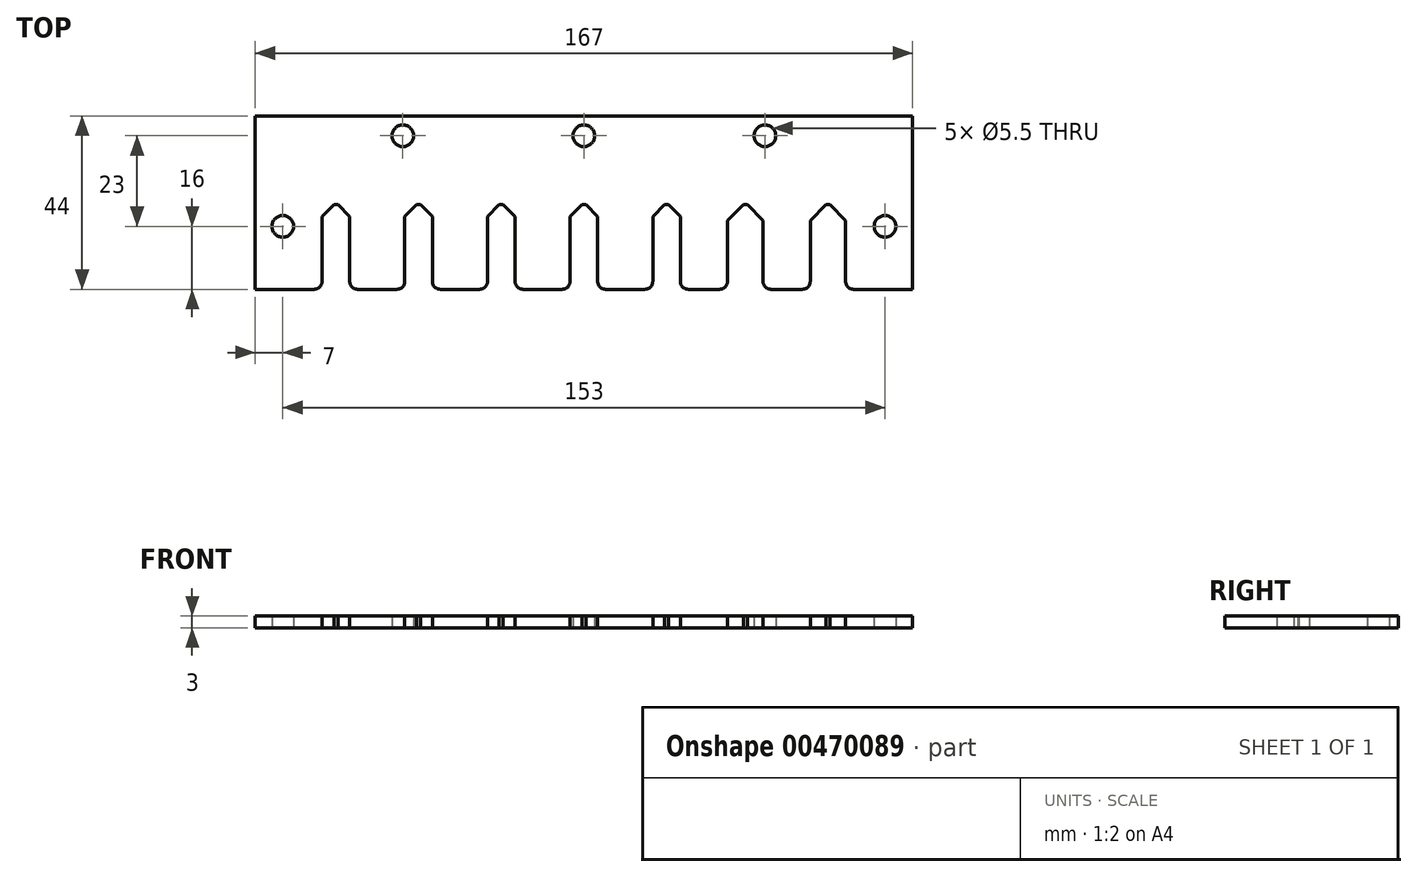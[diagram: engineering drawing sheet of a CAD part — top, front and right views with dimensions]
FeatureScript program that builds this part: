
annotation { "Feature Type Name" : "Feature", "Feature Type Description" : "" }
export const myFeature = defineFeature(function(context is Context, id is Id, definition is map)
    precondition{}
    {
        {
            var Q0;
            Q0=qCreatedBy(makeId("Top.planeOp"),FACE);
            var sketch = newSketch(context, id + "F0", { "sketchPlane" : qUnion([Q0])});
            skLineSegment(sketch, "E0", {"start": v(0, 0) * mm, "end": v(0, 44) * mm});
            skLineSegment(sketch, "E1", {"start": v(0, 44) * mm, "end": v(167, 44) * mm});
            skLineSegment(sketch, "E2", {"start": v(167, 44) * mm, "end": v(167, 0) * mm});
            skLineSegment(sketch, "E3", {"start": v(167, 0) * mm, "end": v(152, 0) * mm});
            skLineSegment(sketch, "E4", {"start": v(150, 2) * mm, "end": v(150, 18) * mm});
            skLineSegment(sketch, "E5", {"start": v(146, 22) * mm, "end": v(145, 22) * mm});
            skLineSegment(sketch, "E6", {"start": v(141, 18) * mm, "end": v(141, 2) * mm});
            skLineSegment(sketch, "E7", {"start": v(139, 0) * mm, "end": v(131, 0) * mm});
            skLineSegment(sketch, "E8", {"start": v(129, 2) * mm, "end": v(129, 18) * mm});
            skLineSegment(sketch, "E9", {"start": v(125, 22) * mm, "end": v(124, 22) * mm});
            skLineSegment(sketch, "E10", {"start": v(120, 18) * mm, "end": v(120, 2) * mm});
            skLineSegment(sketch, "E11", {"start": v(118, 0) * mm, "end": v(110, 0) * mm});
            skLineSegment(sketch, "E12", {"start": v(108, 2) * mm, "end": v(108, 19) * mm});
            skLineSegment(sketch, "E13", {"start": v(105, 22) * mm, "end": v(104, 22) * mm});
            skLineSegment(sketch, "E14", {"start": v(101, 19) * mm, "end": v(101, 2) * mm});
            skLineSegment(sketch, "E15", {"start": v(99, 0) * mm, "end": v(89, 0) * mm});
            skLineSegment(sketch, "E16", {"start": v(87, 2) * mm, "end": v(87, 19) * mm});
            skLineSegment(sketch, "E17", {"start": v(84, 22) * mm, "end": v(83, 22) * mm});
            skLineSegment(sketch, "E18", {"start": v(80, 19) * mm, "end": v(80, 2) * mm});
            skLineSegment(sketch, "E19", {"start": v(78, 0) * mm, "end": v(68, 0) * mm});
            skLineSegment(sketch, "E20", {"start": v(66, 2) * mm, "end": v(66, 19) * mm});
            skLineSegment(sketch, "E21", {"start": v(63, 22) * mm, "end": v(62, 22) * mm});
            skLineSegment(sketch, "E22", {"start": v(59, 19) * mm, "end": v(59, 2) * mm});
            skLineSegment(sketch, "E23", {"start": v(57, 0) * mm, "end": v(47, 0) * mm});
            skLineSegment(sketch, "E24", {"start": v(45, 2) * mm, "end": v(45, 19) * mm});
            skLineSegment(sketch, "E25", {"start": v(42, 22) * mm, "end": v(41, 22) * mm});
            skLineSegment(sketch, "E26", {"start": v(38, 19) * mm, "end": v(38, 2) * mm});
            skLineSegment(sketch, "E27", {"start": v(36, 0) * mm, "end": v(26, 0) * mm});
            skLineSegment(sketch, "E28", {"start": v(24, 2) * mm, "end": v(24, 19) * mm});
            skLineSegment(sketch, "E29", {"start": v(21, 22) * mm, "end": v(20, 22) * mm});
            skLineSegment(sketch, "E30", {"start": v(17, 19) * mm, "end": v(17, 2) * mm});
            skLineSegment(sketch, "E31", {"start": v(15, 0) * mm, "end": v(0, 0) * mm});
            skCircle(sketch, "E32", {"center": v(160, 16) * mm, "radius": 2.75 * mm});
            skCircle(sketch, "E33", {"center": v(129.5, 39) * mm, "radius": 2.75 * mm});
            skCircle(sketch, "E34", {"center": v(37.5, 39) * mm, "radius": 2.75 * mm});
            skPoint(sketch, "E35.centerSnap0", {"position": v(20.5, 22) * mm});
            skCircle(sketch, "E36", {"center": v(20.5, 19) * mm, "radius": 3 * mm, "construction": true});
            skLineSegment(sketch, "E37", {"start": v(20.5, 22) * mm, "end": v(20.5, 0) * mm, "construction": true});
            skCircle(sketch, "E38", {"center": v(20.5, 19) * mm, "radius": 5 * mm, "construction": true});
            skCircle(sketch, "E39", {"center": v(41.5, 19) * mm, "radius": 3 * mm, "construction": true});
            skPoint(sketch, "E39.centerSnap0", {"position": v(41.5, 22) * mm});
            skCircle(sketch, "E40", {"center": v(41.5, 19) * mm, "radius": 5 * mm, "construction": true});
            skPoint(sketch, "E41.visualSharp", {"position": v(17, 0) * mm});
            skArc(sketch, "E41.filletArc", {"start": v(15, 0) * mm, "mid": v(16.41, 0.59) * mm, "end": v(17, 2) * mm});
            skPoint(sketch, "E42.visualSharp", {"position": v(24, 0) * mm});
            skArc(sketch, "E42.filletArc", {"start": v(24, 2) * mm, "mid": v(24.59, 0.59) * mm, "end": v(26, 0) * mm});
            skPoint(sketch, "E43.visualSharp", {"position": v(38, 0) * mm});
            skArc(sketch, "E43.filletArc", {"start": v(36, 0) * mm, "mid": v(37.41, 0.59) * mm, "end": v(38, 2) * mm});
            skPoint(sketch, "E44.visualSharp", {"position": v(45, 0) * mm});
            skArc(sketch, "E44.filletArc", {"start": v(45, 2) * mm, "mid": v(45.59, 0.59) * mm, "end": v(47, 0) * mm});
            skPoint(sketch, "E45.visualSharp", {"position": v(59, 0) * mm});
            skArc(sketch, "E45.filletArc", {"start": v(57, 0) * mm, "mid": v(58.41, 0.59) * mm, "end": v(59, 2) * mm});
            skPoint(sketch, "E46.visualSharp", {"position": v(66, 0) * mm});
            skArc(sketch, "E46.filletArc", {"start": v(66, 2) * mm, "mid": v(66.59, 0.59) * mm, "end": v(68, 0) * mm});
            skPoint(sketch, "E47.visualSharp", {"position": v(80, 0) * mm});
            skArc(sketch, "E47.filletArc", {"start": v(78, 0) * mm, "mid": v(79.41, 0.59) * mm, "end": v(80, 2) * mm});
            skPoint(sketch, "E48.visualSharp", {"position": v(87, 0) * mm});
            skArc(sketch, "E48.filletArc", {"start": v(87, 2) * mm, "mid": v(87.59, 0.59) * mm, "end": v(89, 0) * mm});
            skPoint(sketch, "E49.visualSharp", {"position": v(101, 0) * mm});
            skArc(sketch, "E49.filletArc", {"start": v(99, 0) * mm, "mid": v(100.41, 0.59) * mm, "end": v(101, 2) * mm});
            skPoint(sketch, "E50.visualSharp", {"position": v(108, 0) * mm});
            skArc(sketch, "E50.filletArc", {"start": v(108, 2) * mm, "mid": v(108.59, 0.59) * mm, "end": v(110, 0) * mm});
            skPoint(sketch, "E51.visualSharp", {"position": v(120, 0) * mm});
            skArc(sketch, "E51.filletArc", {"start": v(118, 0) * mm, "mid": v(119.41, 0.59) * mm, "end": v(120, 2) * mm});
            skPoint(sketch, "E52.visualSharp", {"position": v(129, 0) * mm});
            skArc(sketch, "E52.filletArc", {"start": v(129, 2) * mm, "mid": v(129.59, 0.59) * mm, "end": v(131, 0) * mm});
            skPoint(sketch, "E53.visualSharp", {"position": v(141, 0) * mm});
            skArc(sketch, "E53.filletArc", {"start": v(139, 0) * mm, "mid": v(140.41, 0.59) * mm, "end": v(141, 2) * mm});
            skPoint(sketch, "E54.visualSharp", {"position": v(150, 0) * mm});
            skArc(sketch, "E54.filletArc", {"start": v(150, 2) * mm, "mid": v(150.59, 0.59) * mm, "end": v(152, 0) * mm});
            skCircle(sketch, "E55", {"center": v(7, 16) * mm, "radius": 2.75 * mm});
            skPoint(sketch, "E56.visualSharp", {"position": v(45, 22) * mm});
            skArc(sketch, "E56.filletArc", {"start": v(45, 19) * mm, "mid": v(44.12, 21.12) * mm, "end": v(42, 22) * mm});
            skPoint(sketch, "E57.visualSharp", {"position": v(38, 22) * mm});
            skArc(sketch, "E57.filletArc", {"start": v(41, 22) * mm, "mid": v(38.88, 21.12) * mm, "end": v(38, 19) * mm});
            skPoint(sketch, "E58.visualSharp", {"position": v(24, 22) * mm});
            skArc(sketch, "E58.filletArc", {"start": v(24, 19) * mm, "mid": v(23.12, 21.12) * mm, "end": v(21, 22) * mm});
            skPoint(sketch, "E59.visualSharp", {"position": v(17, 22) * mm});
            skArc(sketch, "E59.filletArc", {"start": v(20, 22) * mm, "mid": v(17.88, 21.12) * mm, "end": v(17, 19) * mm});
            skPoint(sketch, "E60.visualSharp", {"position": v(59, 22) * mm});
            skArc(sketch, "E60.filletArc", {"start": v(62, 22) * mm, "mid": v(59.88, 21.12) * mm, "end": v(59, 19) * mm});
            skPoint(sketch, "E61.visualSharp", {"position": v(66, 22) * mm});
            skArc(sketch, "E61.filletArc", {"start": v(66, 19) * mm, "mid": v(65.12, 21.12) * mm, "end": v(63, 22) * mm});
            skPoint(sketch, "E62.visualSharp", {"position": v(80, 22) * mm});
            skArc(sketch, "E62.filletArc", {"start": v(83, 22) * mm, "mid": v(80.88, 21.12) * mm, "end": v(80, 19) * mm});
            skPoint(sketch, "E63.visualSharp", {"position": v(87, 22) * mm});
            skArc(sketch, "E63.filletArc", {"start": v(87, 19) * mm, "mid": v(86.12, 21.12) * mm, "end": v(84, 22) * mm});
            skPoint(sketch, "E64.visualSharp", {"position": v(101, 22) * mm});
            skArc(sketch, "E64.filletArc", {"start": v(104, 22) * mm, "mid": v(101.88, 21.12) * mm, "end": v(101, 19) * mm});
            skPoint(sketch, "E65.visualSharp", {"position": v(108, 22) * mm});
            skArc(sketch, "E65.filletArc", {"start": v(108, 19) * mm, "mid": v(107.12, 21.12) * mm, "end": v(105, 22) * mm});
            skPoint(sketch, "E66", {"position": v(62.5, 22) * mm});
            skPoint(sketch, "E67", {"position": v(83.5, 22) * mm});
            skCircle(sketch, "E68", {"center": v(83.5, 19) * mm, "radius": 3 * mm, "construction": true});
            skCircle(sketch, "E69", {"center": v(83.5, 19) * mm, "radius": 5 * mm, "construction": true});
            skCircle(sketch, "E70", {"center": v(62.5, 19) * mm, "radius": 3 * mm, "construction": true});
            skCircle(sketch, "E71", {"center": v(62.5, 19) * mm, "radius": 5 * mm, "construction": true});
            skPoint(sketch, "E72", {"position": v(104.5, 22) * mm});
            skCircle(sketch, "E73", {"center": v(104.5, 19) * mm, "radius": 3 * mm, "construction": true});
            skCircle(sketch, "E74", {"center": v(104.5, 19) * mm, "radius": 5 * mm, "construction": true});
            skCircle(sketch, "E75", {"center": v(145.5, 19) * mm, "radius": 3 * mm, "construction": true});
            skCircle(sketch, "E76", {"center": v(145.5, 19) * mm, "radius": 7 * mm, "construction": true});
            skPoint(sketch, "E77.visualSharp", {"position": v(141, 22) * mm});
            skArc(sketch, "E77.filletArc", {"start": v(145, 22) * mm, "mid": v(142.17, 20.83) * mm, "end": v(141, 18) * mm});
            skArc(sketch, "E78.filletArc", {"start": v(150, 18) * mm, "mid": v(148.83, 20.83) * mm, "end": v(146, 22) * mm});
            skPoint(sketch, "E79.visualSharp", {"position": v(129, 22) * mm});
            skArc(sketch, "E79.filletArc", {"start": v(129, 18) * mm, "mid": v(127.83, 20.83) * mm, "end": v(125, 22) * mm});
            skPoint(sketch, "E80.visualSharp", {"position": v(120, 22) * mm});
            skArc(sketch, "E80.filletArc", {"start": v(124, 22) * mm, "mid": v(121.17, 20.83) * mm, "end": v(120, 18) * mm});
            skPoint(sketch, "E81", {"position": v(145.5, 22) * mm});
            skCircle(sketch, "E82", {"center": v(124.5, 19) * mm, "radius": 3 * mm, "construction": true});
            skPoint(sketch, "E82.centerSnap0", {"position": v(124.5, 22) * mm});
            skCircle(sketch, "E83", {"center": v(124.5, 19) * mm, "radius": 7 * mm, "construction": true});
            skLineSegment(sketch, "E84", {"start": v(83.5, 44) * mm, "end": v(83.5, 31) * mm, "construction": true});
            skCircle(sketch, "E85", {"center": v(83.5, 39) * mm, "radius": 2.75 * mm});
            skLineSegment(sketch, "E86", {"start": v(20.5, 22) * mm, "end": v(17, 18.5) * mm});
            skLineSegment(sketch, "E87", {"start": v(20.5, 22) * mm, "end": v(24, 18.5) * mm});
            skCircle(sketch, "E88", {"center": v(20.5, 17.76) * mm, "radius": 3 * mm, "construction": true});
            skLineSegment(sketch, "E89", {"start": v(20, 21.5) * mm, "end": v(21, 21.5) * mm});
            skLineSegment(sketch, "E90.1.0.0", {"start": v(41.5, 22) * mm, "end": v(38, 18.5) * mm});
            skLineSegment(sketch, "E90.1.0.1", {"start": v(41.5, 22) * mm, "end": v(45, 18.5) * mm});
            skLineSegment(sketch, "E90.1.0.2", {"start": v(41, 21.5) * mm, "end": v(42, 21.5) * mm});
            skLineSegment(sketch, "E90.2.0.0", {"start": v(62.5, 22) * mm, "end": v(59, 18.5) * mm});
            skLineSegment(sketch, "E90.2.0.1", {"start": v(62.5, 22) * mm, "end": v(66, 18.5) * mm});
            skLineSegment(sketch, "E90.2.0.2", {"start": v(62, 21.5) * mm, "end": v(63, 21.5) * mm});
            skLineSegment(sketch, "E90.3.0.0", {"start": v(83.5, 22) * mm, "end": v(80, 18.5) * mm});
            skLineSegment(sketch, "E90.3.0.1", {"start": v(83.5, 22) * mm, "end": v(87, 18.5) * mm});
            skLineSegment(sketch, "E90.3.0.2", {"start": v(83, 21.5) * mm, "end": v(84, 21.5) * mm});
            skLineSegment(sketch, "E90.direction1", {"start": v(17, 18.5) * mm, "end": v(38, 18.5) * mm, "construction": true});
            skLineSegment(sketch, "E91.1.0.0", {"start": v(104.5, 22) * mm, "end": v(101, 18.5) * mm});
            skLineSegment(sketch, "E91.1.0.1", {"start": v(104, 21.5) * mm, "end": v(105, 21.5) * mm});
            skLineSegment(sketch, "E91.1.0.2", {"start": v(104.5, 22) * mm, "end": v(108, 18.5) * mm});
            skLineSegment(sketch, "E91.direction1", {"start": v(80, 18.5) * mm, "end": v(101, 18.5) * mm, "construction": true});
            skLineSegment(sketch, "E92", {"start": v(124.5, 22) * mm, "end": v(120, 17.5) * mm});
            skLineSegment(sketch, "E93", {"start": v(124.5, 22) * mm, "end": v(129, 17.5) * mm});
            skLineSegment(sketch, "E94", {"start": v(124, 21.5) * mm, "end": v(125, 21.5) * mm});
            skLineSegment(sketch, "E95.1.0.0", {"start": v(145.5, 22) * mm, "end": v(141, 17.5) * mm});
            skLineSegment(sketch, "E95.1.0.1", {"start": v(145, 21.5) * mm, "end": v(146, 21.5) * mm});
            skLineSegment(sketch, "E95.1.0.2", {"start": v(145.5, 22) * mm, "end": v(150, 17.5) * mm});
            skLineSegment(sketch, "E95.direction1", {"start": v(120, 17.5) * mm, "end": v(141, 17.5) * mm, "construction": true});
            skSolve(sketch);
        }
        {
            var Q0;
            Q0=makeQuery(id+"F0.imprint","IMPRINT",FACE,{"disambiguationData":[TD([[makeQuery(id+"F0.imprint","IMPRINT",EDGE,{"derivedFrom":sQuery(id+"F0.wireOp",EDGE,"E0")}),-1.0]])]});
            var Q1;
            {var subQ0=sQuery(id+"F0.wireOp",EDGE,"E59.filletArc");Q1=makeQuery(id+"F0.imprint","IMPRINT",FACE,{"disambiguationData":[TD([[makeQuery(id+"F0.imprint","IMPRINT",EDGE,{"derivedFrom":subQ0}),1.0]])]});}
            var Q2;
            {var subQ0=sQuery(id+"F0.wireOp",EDGE,"E58.filletArc");Q2=makeQuery(id+"F0.imprint","IMPRINT",FACE,{"disambiguationData":[TD([[makeQuery(id+"F0.imprint","IMPRINT",EDGE,{"derivedFrom":subQ0}),1.0]])]});}
            var Q3;
            {var subQ3=sQuery(id+"F0.wireOp",EDGE,"E89");Q3=makeQuery(id+"F0.imprint","IMPRINT",FACE,{"disambiguationData":[TD([[makeQuery(id+"F0.imprint","IMPRINT",EDGE,{"derivedFrom":subQ3}),1.0]])]});}
            var Q4;
            {var subQ4=sQuery(id+"F0.wireOp",EDGE,"E57.filletArc");Q4=makeQuery(id+"F0.imprint","IMPRINT",FACE,{"disambiguationData":[TD([[makeQuery(id+"F0.imprint","IMPRINT",EDGE,{"derivedFrom":subQ4}),1.0]])]});}
            var Q5;
            {var subQ3=sQuery(id+"F0.wireOp",EDGE,"E90.1.0.2");Q5=makeQuery(id+"F0.imprint","IMPRINT",FACE,{"disambiguationData":[TD([[makeQuery(id+"F0.imprint","IMPRINT",EDGE,{"derivedFrom":subQ3}),1.0]])]});}
            var Q6;
            {var subQ4=sQuery(id+"F0.wireOp",EDGE,"E56.filletArc");Q6=makeQuery(id+"F0.imprint","IMPRINT",FACE,{"disambiguationData":[TD([[makeQuery(id+"F0.imprint","IMPRINT",EDGE,{"derivedFrom":subQ4}),1.0]])]});}
            var Q7;
            {var subQ4=sQuery(id+"F0.wireOp",EDGE,"E62.filletArc");Q7=makeQuery(id+"F0.imprint","IMPRINT",FACE,{"disambiguationData":[TD([[makeQuery(id+"F0.imprint","IMPRINT",EDGE,{"derivedFrom":subQ4}),1.0]])]});}
            var Q8;
            {var subQ3=sQuery(id+"F0.wireOp",EDGE,"E90.3.0.2");Q8=makeQuery(id+"F0.imprint","IMPRINT",FACE,{"disambiguationData":[TD([[makeQuery(id+"F0.imprint","IMPRINT",EDGE,{"derivedFrom":subQ3}),1.0]])]});}
            var Q9;
            {var subQ4=sQuery(id+"F0.wireOp",EDGE,"E63.filletArc");Q9=makeQuery(id+"F0.imprint","IMPRINT",FACE,{"disambiguationData":[TD([[makeQuery(id+"F0.imprint","IMPRINT",EDGE,{"derivedFrom":subQ4}),1.0]])]});}
            var Q10;
            {var subQ0=sQuery(id+"F0.wireOp",EDGE,"E64.filletArc");Q10=makeQuery(id+"F0.imprint","IMPRINT",FACE,{"disambiguationData":[TD([[makeQuery(id+"F0.imprint","IMPRINT",EDGE,{"derivedFrom":subQ0}),1.0]])]});}
            var Q11;
            {var subQ3=sQuery(id+"F0.wireOp",EDGE,"E91.1.0.1");Q11=makeQuery(id+"F0.imprint","IMPRINT",FACE,{"disambiguationData":[TD([[makeQuery(id+"F0.imprint","IMPRINT",EDGE,{"derivedFrom":subQ3}),1.0]])]});}
            var Q12;
            {var subQ0=sQuery(id+"F0.wireOp",EDGE,"E65.filletArc");Q12=makeQuery(id+"F0.imprint","IMPRINT",FACE,{"disambiguationData":[TD([[makeQuery(id+"F0.imprint","IMPRINT",EDGE,{"derivedFrom":subQ0}),1.0]])]});}
            var Q13;
            {var subQ4=sQuery(id+"F0.wireOp",EDGE,"E80.filletArc");Q13=makeQuery(id+"F0.imprint","IMPRINT",FACE,{"disambiguationData":[TD([[makeQuery(id+"F0.imprint","IMPRINT",EDGE,{"derivedFrom":subQ4}),1.0]])]});}
            var Q14;
            {var subQ3=sQuery(id+"F0.wireOp",EDGE,"E94");Q14=makeQuery(id+"F0.imprint","IMPRINT",FACE,{"disambiguationData":[TD([[makeQuery(id+"F0.imprint","IMPRINT",EDGE,{"derivedFrom":subQ3}),1.0]])]});}
            var Q15;
            {var subQ4=sQuery(id+"F0.wireOp",EDGE,"E79.filletArc");Q15=makeQuery(id+"F0.imprint","IMPRINT",FACE,{"disambiguationData":[TD([[makeQuery(id+"F0.imprint","IMPRINT",EDGE,{"derivedFrom":subQ4}),1.0]])]});}
            var Q16;
            {var subQ4=sQuery(id+"F0.wireOp",EDGE,"E77.filletArc");Q16=makeQuery(id+"F0.imprint","IMPRINT",FACE,{"disambiguationData":[TD([[makeQuery(id+"F0.imprint","IMPRINT",EDGE,{"derivedFrom":subQ4}),1.0]])]});}
            var Q17;
            {var subQ3=sQuery(id+"F0.wireOp",EDGE,"E95.1.0.1");Q17=makeQuery(id+"F0.imprint","IMPRINT",FACE,{"disambiguationData":[TD([[makeQuery(id+"F0.imprint","IMPRINT",EDGE,{"derivedFrom":subQ3}),1.0]])]});}
            var Q18;
            {var subQ4=sQuery(id+"F0.wireOp",EDGE,"E78.filletArc");Q18=makeQuery(id+"F0.imprint","IMPRINT",FACE,{"disambiguationData":[TD([[makeQuery(id+"F0.imprint","IMPRINT",EDGE,{"derivedFrom":subQ4}),1.0]])]});}
            var Q19;
            {var subQ4=sQuery(id+"F0.wireOp",EDGE,"E60.filletArc");Q19=makeQuery(id+"F0.imprint","IMPRINT",FACE,{"disambiguationData":[TD([[makeQuery(id+"F0.imprint","IMPRINT",EDGE,{"derivedFrom":subQ4}),1.0]])]});}
            var Q20;
            {var subQ3=sQuery(id+"F0.wireOp",EDGE,"E90.2.0.2");Q20=makeQuery(id+"F0.imprint","IMPRINT",FACE,{"disambiguationData":[TD([[makeQuery(id+"F0.imprint","IMPRINT",EDGE,{"derivedFrom":subQ3}),1.0]])]});}
            var Q21;
            {var subQ0=sQuery(id+"F0.wireOp",EDGE,"E61.filletArc");Q21=makeQuery(id+"F0.imprint","IMPRINT",FACE,{"disambiguationData":[TD([[makeQuery(id+"F0.imprint","IMPRINT",EDGE,{"derivedFrom":subQ0}),1.0]])]});}
            extrude(context, id + "F1", {"entities" : qUnion([Q0, Q1, Q2, Q3, Q4, Q5, Q6, Q7, Q8, Q9, Q10, Q11, Q12, Q13, Q14, Q15, Q16, Q17, Q18, Q19, Q20, Q21]), "offsetDistance" : 25 * mm, "depth" : 3 * mm});
        }
    });
